# Revit family: HL_RU_Drainage and inspection chamber_HL635N-A-221005
name_source: partatom
category: Instalační zařizovací předměty
units: mm (PartAtom-declared; Revit-internal decimal feet)

## family parameters
Bod výpočtu místnosti = Ano
Kóta kulaté spojky = Použít průměr
Nadpis OmniClass = Deck Waste Water Drains
Ořezat dutým tvarem při načtení = Ne
Sdílené = Ne
Typ dílu = Normální
Vždy vertikální = Ano
Založené na pracovní rovině = Ne
Číslo OmniClass = 23.70.50.21.24.14

## types (1)
- HL_Дренажный и инспекционный колодец для_HL635N
    EAN = 9003076032228
    Indexovaná poznámka = HL635N
    Komentáře k typům = Дренажный и инспекционный колодец для "зелёных" и эксплуатируемых кровель и кровель с пригрузом из гравия, с пластиковым подрамником и пластиковой решёткой
    Model = HL635N
    Popis = крыша
    Přípoj CW = Ne
    Přípoj HW = Ne
    Přípoj odpadních dílů = Ano
    Přípoj ventilace = Ne
    URL = http://www.hutterer-lechner.com
    Výchozí výška = 0 mm  [stored 0 ft]
    Výrobce = HL Hutterer & Lechner GmbH
    ВЕС = 2,45kg
    ВЫСОТА МОНТАЖА = 70 - 205mm
    МАКСИМАЛЬНАЯ НАГРУЗКА КЛАССА = K3 - max. 300kg
    МАТЕРИАЛ = EPS/ PP
    НОМИНАЛЬНЫЙ ДИАМЕТР = 350 mm
    НОРМЫ = EN1986-3/ EN1253-2
    РАЗМЕР = 390x390x205mm
    РЕШЁТКА = Kunststoff 368x368mm

note: [stored X ft] marks values corroborated as IEEE doubles in the binary element streams (Revit-internal decimal feet)

## geometry (parser evidence)
native form markers: Sweep x3
no freeform markers — native parametric forms only
